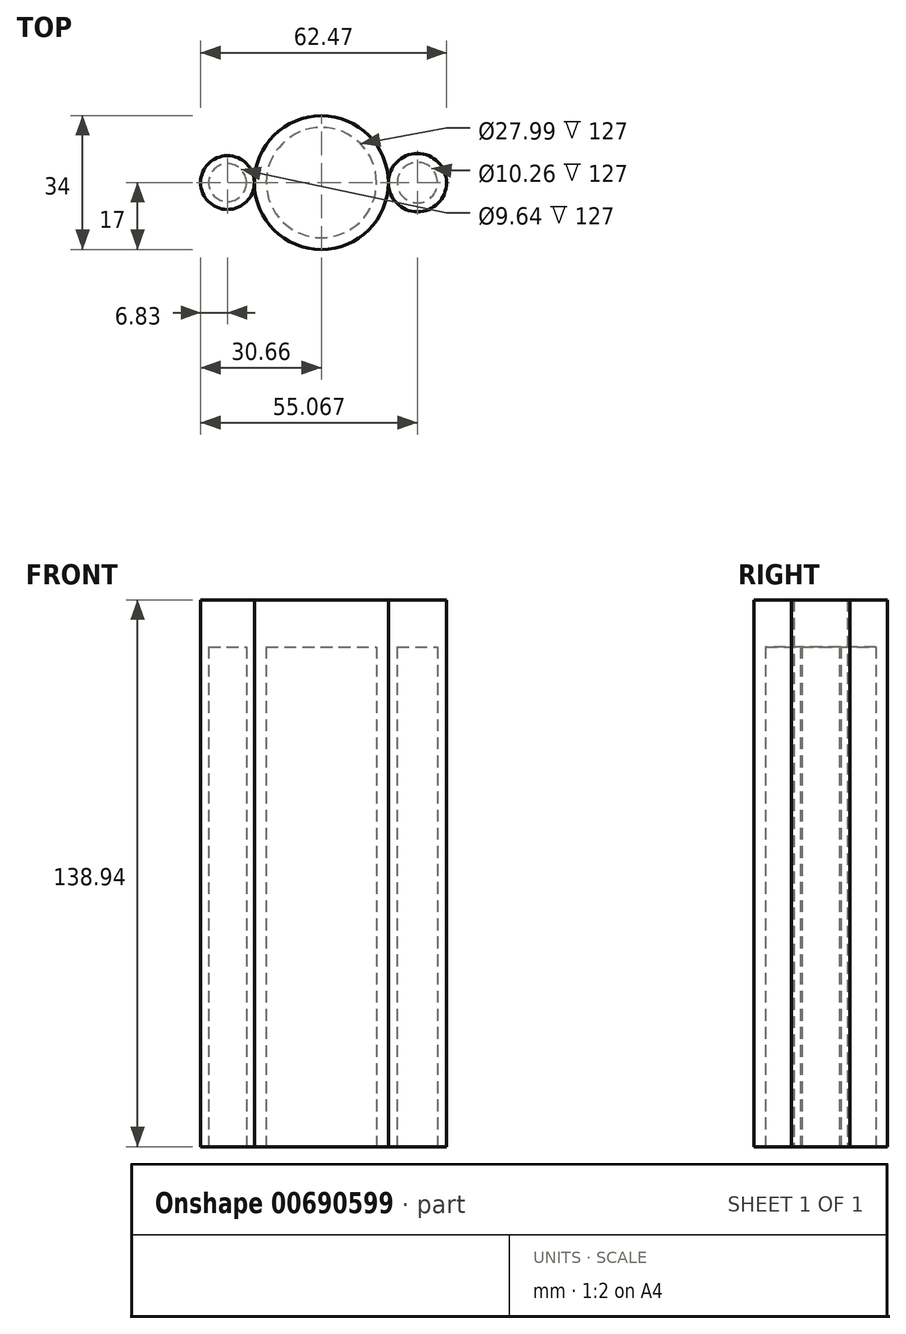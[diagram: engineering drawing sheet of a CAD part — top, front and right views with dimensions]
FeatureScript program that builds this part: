
annotation { "Feature Type Name" : "Feature", "Feature Type Description" : "" }
export const myFeature = defineFeature(function(context is Context, id is Id, definition is map)
    precondition{}
    {
        {
            var Q0;
            Q0=qCreatedBy(makeId("Top.planeOp"),FACE);
            var sketch = newSketch(context, id + "F0", { "sketchPlane" : qUnion([Q0])});
            skCircle(sketch, "E0", {"center": v(0, 0) * mm, "radius": 17 * mm});
            skCircle(sketch, "E1", {"center": v(24.4, 0) * mm, "radius": 7.4 * mm});
            skCircle(sketch, "E2", {"center": v(-23.83, 0) * mm, "radius": 6.83 * mm});
            skSolve(sketch);
        }
        {
            var Q0;
            {var subQ0=sQuery(id+"F0.wireOp",EDGE,"E0");var subQ1=makeQuery(id+"F0.imprint","INTERSECT",VERTEX,{"derivedFrom":[subQ0,sQuery(id+"F0.wireOp",EDGE,"E1")]});Q0=makeQuery(id+"F0.imprint","IMPRINT",FACE,{"disambiguationData":[TD([[makeQuery(id+"F0.imprint","IMPRINT",EDGE,{"disambiguationData":[TD([[subQ1,-1.0]])],"derivedFrom":subQ0}),1.0]])]});}
            var Q1;
            Q1=makeQuery(id+"F0.imprint","IMPRINT",FACE,{"disambiguationData":[TD([[makeQuery(id+"F0.imprint","IMPRINT",EDGE,{"derivedFrom":sQuery(id+"F0.wireOp",EDGE,"E1")}),1.0]])]});
            var Q2;
            Q2=makeQuery(id+"F0.imprint","IMPRINT",FACE,{"disambiguationData":[TD([[makeQuery(id+"F0.imprint","IMPRINT",EDGE,{"derivedFrom":sQuery(id+"F0.wireOp",EDGE,"E2")}),1.0]])]});
            extrude(context, id + "F1", {"entities" : qUnion([Q0, Q1, Q2]), "depth" : 138.94 * mm, "offsetDistance" : 25.4 * mm});
        }
        {
            var Q0;
            Q0=makeQuery(id+"F1.opExtrude","CAP_FACE",FACE,{"disambiguationData":[OSD([sQuery(id+"F0.wireOp",EDGE,"E0")])],"isStart":true});
            var sketch = newSketch(context, id + "F2", { "sketchPlane" : qUnion([Q0])});
            skCircle(sketch, "E3", {"center": v(0, 0) * mm, "radius": 14 * mm});
            skSolve(sketch);
        }
        {
            var Q0;
            Q0=makeQuery(id+"F2.imprint","IMPRINT",FACE,{"disambiguationData":[TD([[makeQuery(id+"F2.imprint","IMPRINT",EDGE,{"derivedFrom":sQuery(id+"F2.wireOp",EDGE,"E3")}),1.0]])]});
            extrude(context, id + "F3", {"entities" : qUnion([Q0]), "operationType" : NewBodyOperationType.REMOVE, "oppositeDirection" : true, "depth" : 127 * mm, "offsetDistance" : 25.4 * mm});
        }
        {
            var Q0;
            Q0=makeQuery(id+"F1.opExtrude","CAP_FACE",FACE,{"disambiguationData":[OSD([sQuery(id+"F0.wireOp",EDGE,"E1")])],"isStart":true});
            var sketch = newSketch(context, id + "F4", { "sketchPlane" : qUnion([Q0])});
            skCircle(sketch, "E4", {"center": v(24.4, 0) * mm, "radius": 5.13 * mm});
            skSolve(sketch);
        }
        {
            var Q0;
            Q0=makeQuery(id+"F4.imprint","IMPRINT",FACE,{"disambiguationData":[TD([[makeQuery(id+"F4.imprint","IMPRINT",EDGE,{"derivedFrom":sQuery(id+"F4.wireOp",EDGE,"E4")}),1.0]])]});
            extrude(context, id + "F5", {"entities" : qUnion([Q0]), "operationType" : NewBodyOperationType.REMOVE, "oppositeDirection" : true, "depth" : 127 * mm, "offsetDistance" : 25.4 * mm});
        }
        {
            var Q0;
            Q0=makeQuery(id+"F1.opExtrude","CAP_FACE",FACE,{"disambiguationData":[OSD([sQuery(id+"F0.wireOp",EDGE,"E2")])],"isStart":true});
            var sketch = newSketch(context, id + "F6", { "sketchPlane" : qUnion([Q0])});
            skCircle(sketch, "E5", {"center": v(-23.83, 0) * mm, "radius": 4.82 * mm});
            skSolve(sketch);
        }
        {
            var Q0;
            Q0=makeQuery(id+"F6.imprint","IMPRINT",FACE,{"disambiguationData":[TD([[makeQuery(id+"F6.imprint","IMPRINT",EDGE,{"derivedFrom":sQuery(id+"F6.wireOp",EDGE,"E5")}),1.0]])]});
            extrude(context, id + "F7", {"entities" : qUnion([Q0]), "operationType" : NewBodyOperationType.REMOVE, "oppositeDirection" : true, "depth" : 127 * mm, "offsetDistance" : 25.4 * mm});
        }
    });
